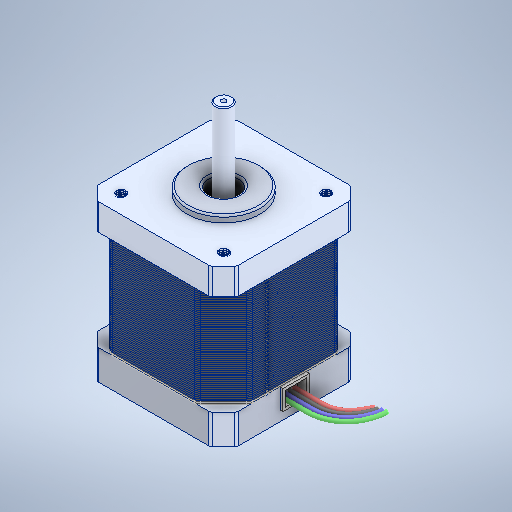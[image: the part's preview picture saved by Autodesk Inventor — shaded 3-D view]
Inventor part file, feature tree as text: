
AUTODESK INVENTOR PART (.ipt)
format: ipt  version: 2025.1 (Build 291241020, 241B)  size: 3,425,792 bytes
history: native  units: in
note: dims shown in document units (in); Inventor stores cm internally (conversion verified against a paired STEP export)
features: other x69, sweep x28, extrude x1, pattern_circular x1, chamfer x1
ambient origin geometry x8: Origin, YZ Plane, XZ Plane, XY Plane, X Axis, Y Axis, Z Axis, Center Point
bodies: Solid1 (feature_tree), Solid2 (feature_tree), Solid3 (feature_tree), Solid4 (feature_tree), Solid5 (feature_tree), Solid6 (feature_tree), Solid7 (feature_tree), Solid8 (feature_tree), Solid9 (feature_tree), Solid10 (feature_tree), Solid11 (feature_tree), Solid12 (feature_tree), Solid13 (feature_tree), Solid14 (feature_tree), Solid15 (feature_tree), Solid16 (feature_tree), Solid17 (feature_tree), Solid18 (feature_tree), Solid19 (feature_tree), Solid20 (feature_tree), Solid21 (feature_tree), Solid22 (feature_tree), Solid23 (feature_tree), Solid24 (feature_tree), Solid25 (feature_tree), Solid26 (feature_tree), Solid27 (feature_tree), Solid28 (feature_tree), Solid29 (feature_tree), Solid30 (feature_tree), Solid31 (feature_tree), Solid32 (feature_tree), Solid33 (feature_tree), Solid34 (feature_tree), Solid35 (feature_tree), Solid36 (feature_tree), Solid37 (feature_tree), Solid38 (feature_tree), Solid39 (feature_tree), Solid40 (feature_tree), Solid41 (feature_tree), Solid42 (feature_tree), Solid43 (feature_tree), Solid44 (feature_tree), Solid45 (feature_tree), Solid46 (feature_tree), Solid47 (feature_tree), Solid48 (feature_tree), Solid49 (feature_tree), Solid50 (feature_tree), Solid51 (feature_tree), Solid52 (feature_tree), Solid53 (feature_tree), Solid54 (feature_tree), Solid55 (feature_tree), Solid56 (feature_tree), Solid57 (feature_tree), Solid58 (feature_tree), Solid59 (feature_tree), Solid60 (feature_tree), Solid61 (feature_tree), Solid62 (feature_tree), Solid63 (feature_tree), Solid64 (feature_tree), Solid65 (feature_tree), Solid66 (feature_tree), Solid67 (feature_tree), Solid68 (feature_tree), Solid69 (feature_tree), Solid70 (feature_tree), Solid71 (feature_tree), Solid72 (feature_tree), Solid73 (feature_tree), Solid74 (feature_tree), Solid75 (feature_tree), Solid76 (feature_tree), Solid77 (feature_tree), Solid78 (feature_tree), Solid79 (feature_tree), Solid80 (feature_tree), Solid81 (feature_tree), Solid82 (feature_tree), Solid83 (feature_tree), Solid84 (feature_tree), Solid85 (feature_tree), Solid86 (feature_tree), Solid87 (feature_tree), Solid88 (feature_tree), Solid89 (feature_tree), Solid90 (feature_tree), Solid91 (feature_tree), Solid92 (feature_tree), Solid93 (feature_tree), Solid94 (feature_tree), Solid95 (feature_tree), Solid96 (feature_tree)
feature tree (100):
  other  "Plane7"
  other  "Plane1"
  other  "Plane2"
  other  "Plane3"
  extrude  "Extrude-Thin1"  [1 undecoded]
  other  "CBORE for M3 Pan Head Machine Screw1[1]"
  other  "CBORE for M3 Pan Head Machine Screw1[2]"
  other  "CBORE for M3 Pan Head Machine Screw1[3]"
  other  "CBORE for M3 Pan Head Machine Screw1[4]"
  other  "CBORE for M3 Pan Head Machine Screw1[5]"
  other  "CBORE for M3 Pan Head Machine Screw1[6]"
  other  "CBORE for M3 Pan Head Machine Screw1[7]"
  other  "CBORE for M3 Pan Head Machine Screw1[8]"
  other  "CBORE for M3 Pan Head Machine Screw1[9]"
  other  "CBORE for M3 Pan Head Machine Screw1[10]"
  other  "CBORE for M3 Pan Head Machine Screw1[11]"
  other  "CBORE for M3 Pan Head Machine Screw1[12]"
  other  "CBORE for M3 Pan Head Machine Screw1[13]"
  other  "CBORE for M3 Pan Head Machine Screw1[14]"
  other  "CBORE for M3 Pan Head Machine Screw1[15]"
  other  "CBORE for M3 Pan Head Machine Screw1[16]"
  other  "CBORE for M3 Pan Head Machine Screw1[17]"
  other  "CBORE for M3 Pan Head Machine Screw1[18]"
  other  "CBORE for M3 Pan Head Machine Screw1[19]"
  other  "CBORE for M3 Pan Head Machine Screw1[20]"
  other  "CBORE for M3 Pan Head Machine Screw1[21]"
  other  "CBORE for M3 Pan Head Machine Screw1[22]"
  other  "CBORE for M3 Pan Head Machine Screw1[23]"
  other  "CBORE for M3 Pan Head Machine Screw1[24]"
  other  "CBORE for M3 Pan Head Machine Screw1[25]"
  other  "CBORE for M3 Pan Head Machine Screw1[26]"
  other  "CBORE for M3 Pan Head Machine Screw1[27]"
  other  "CBORE for M3 Pan Head Machine Screw1[28]"
  other  "CBORE for M3 Pan Head Machine Screw1[29]"
  other  "CBORE for M3 Pan Head Machine Screw1[30]"
  other  "CBORE for M3 Pan Head Machine Screw1[31]"
  other  "CBORE for M3 Pan Head Machine Screw1[32]"
  other  "CBORE for M3 Pan Head Machine Screw1[33]"
  other  "CBORE for M3 Pan Head Machine Screw1[34]"
  other  "CBORE for M3 Pan Head Machine Screw1[35]"
  other  "CBORE for M3 Pan Head Machine Screw1[36]"
  other  "CBORE for M3 Pan Head Machine Screw1[37]"
  other  "CBORE for M3 Pan Head Machine Screw1[38]"
  other  "CBORE for M3 Pan Head Machine Screw1[39]"
  other  "CBORE for M3 Pan Head Machine Screw1[40]"
  other  "CBORE for M3 Pan Head Machine Screw1[41]"
  other  "CBORE for M3 Pan Head Machine Screw1[42]"
  other  "CBORE for M3 Pan Head Machine Screw1[43]"
  other  "CBORE for M3 Pan Head Machine Screw1[44]"
  other  "CBORE for M3 Pan Head Machine Screw1[45]"
  other  "CBORE for M3 Pan Head Machine Screw1[46]"
  other  "CBORE for M3 Pan Head Machine Screw1[47]"
  other  "CBORE for M3 Pan Head Machine Screw1[48]"
  other  "CBORE for M3 Pan Head Machine Screw1[49]"
  other  "CBORE for M3 Pan Head Machine Screw1[50]"
  other  "CBORE for M3 Pan Head Machine Screw1[51]"
  other  "CBORE for M3 Pan Head Machine Screw1[52]"
  other  "CBORE for M3 Pan Head Machine Screw1[53]"
  other  "CBORE for M3 Pan Head Machine Screw1[54]"
  other  "CBORE for M3 Pan Head Machine Screw1[55]"
  other  "CBORE for M3 Pan Head Machine Screw1[56]"
  other  "CBORE for M3 Pan Head Machine Screw1[57]"
  other  "CBORE for M3 Pan Head Machine Screw1[58]"
  other  "CBORE for M3 Pan Head Machine Screw1[59]"
  other  "CBORE for M3 Pan Head Machine Screw1[60]"
  other  "CBORE for M3 Pan Head Machine Screw1[61]"
  pattern_circular  "CirPattern3"
  chamfer  "Chamfer4"  [1 undecoded]
  other  "CirPattern2[1]"
  other  "CirPattern2[2]"
  other  "CirPattern2[3]"
  sweep  "Sweep4[1]"
  sweep  "Sweep4[2]"
  sweep  "Sweep4[3]"
  sweep  "Sweep4[4]"
  sweep  "Sweep4[5]"
  sweep  "Sweep4[6]"
  sweep  "Sweep4[7]"
  sweep  "Sweep4[8]"
  sweep  "Sweep4[9]"
  sweep  "Sweep4[10]"
  sweep  "Sweep4[11]"
  sweep  "Sweep4[12]"
  sweep  "Sweep4[13]"
  sweep  "Sweep4[14]"
  sweep  "Sweep4[15]"
  sweep  "Sweep4[16]"
  sweep  "Sweep4[17]"
  sweep  "Sweep4[18]"
  sweep  "Sweep4[19]"
  sweep  "Sweep4[20]"
  sweep  "Sweep4[21]"
  sweep  "Sweep4[22]"
  sweep  "Sweep4[23]"
  sweep  "Sweep4[24]"
  sweep  "Sweep5[1]"
  sweep  "Sweep5[2]"
  sweep  "Sweep5[3]"
  sweep  "Sweep5[4]"
  other  "Ø1.5 (1.5) Diameter Hole2"
note: 2 required parameter values undecoded (feature->parameter linkage not recoverable at this tier; creation-order binding heuristic only, values carry confidence <= 0.55)
